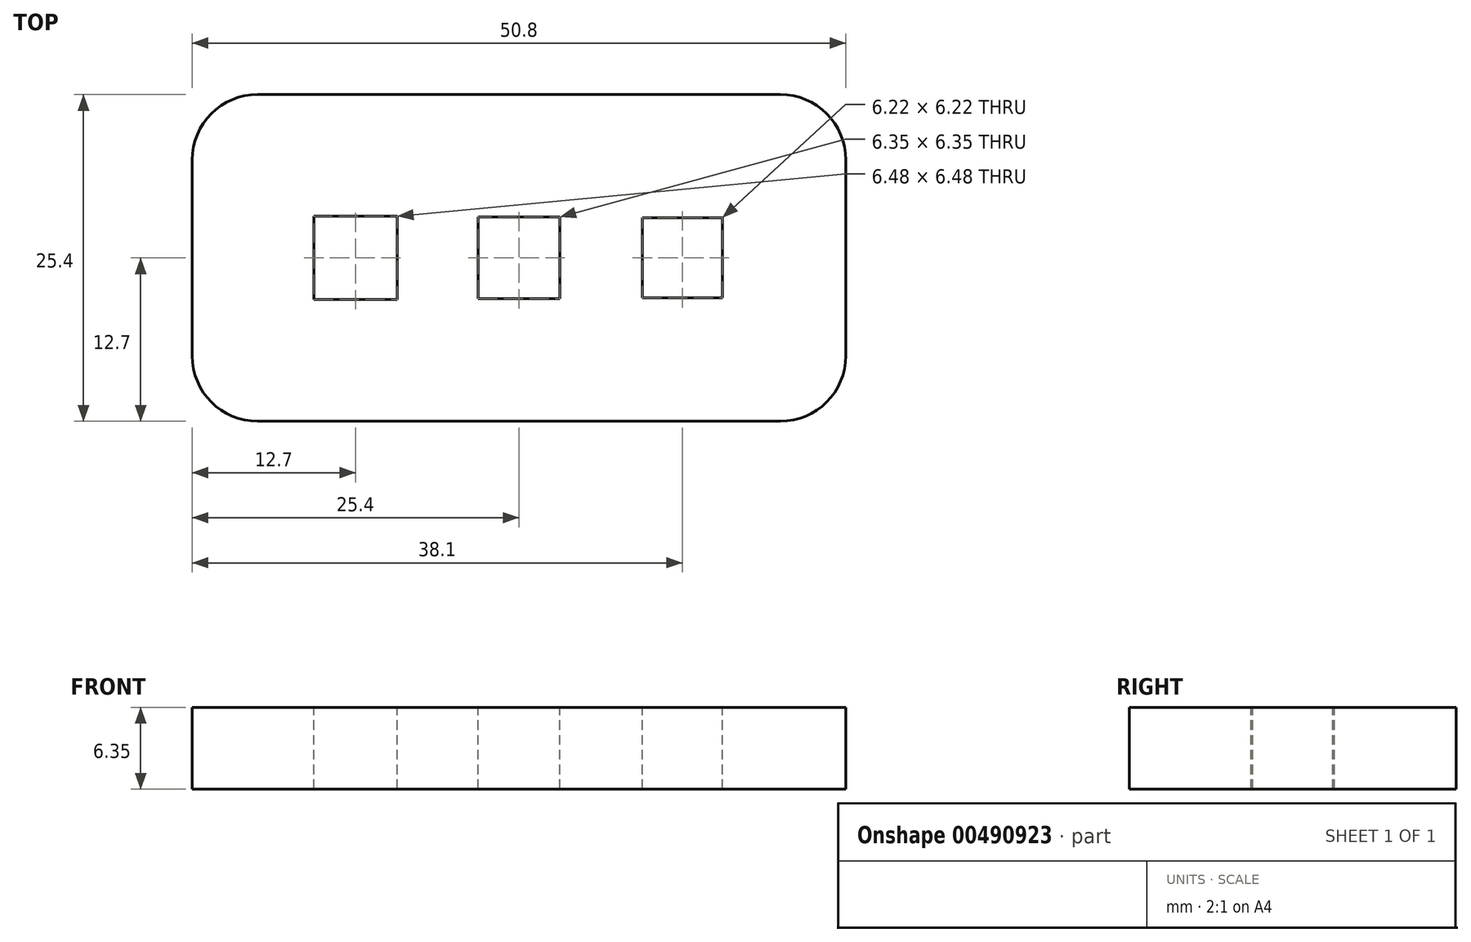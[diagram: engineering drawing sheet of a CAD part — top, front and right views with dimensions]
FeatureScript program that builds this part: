
annotation { "Feature Type Name" : "Feature", "Feature Type Description" : "" }
export const myFeature = defineFeature(function(context is Context, id is Id, definition is map)
    precondition{}
    {
        {
            var Q0;
            Q0=qCreatedBy(makeId("Top.planeOp"),FACE);
            var sketch = newSketch(context, id + "F0", { "sketchPlane" : qUnion([Q0])});
            skLineSegment(sketch, "E0", {"start": v(0, 0) * mm, "end": v(50.8, 0) * mm});
            skLineSegment(sketch, "E1", {"start": v(50.8, 0) * mm, "end": v(50.8, 25.4) * mm});
            skLineSegment(sketch, "E2", {"start": v(50.8, 25.4) * mm, "end": v(0, 25.4) * mm});
            skLineSegment(sketch, "E3", {"start": v(0, 25.4) * mm, "end": v(0, 0) * mm});
            skSolve(sketch);
        }
        {
            var Q0;
            Q0 = qSketchRegion(id + "F0", true);
            extrude(context, id + "F1", {"entities" : qUnion([Q0]), "depth" : 6.35 * mm});
        }
        {
            var Q0;
            Q0=makeQuery(id+"F1.opExtrude","CAP_FACE",FACE,{"disambiguationData":[OSD([sQuery(id+"F0.wireOp",EDGE,"E0"),sQuery(id+"F0.wireOp",EDGE,"E1"),sQuery(id+"F0.wireOp",EDGE,"E2"),sQuery(id+"F0.wireOp",EDGE,"E3")])],"isStart":false});
            var sketch = newSketch(context, id + "F2", { "sketchPlane" : qUnion([Q0])});
            skLineSegment(sketch, "E4", {"start": v(50.8, 12.7) * mm, "end": v(0, 12.7) * mm, "construction": true});
            skLineSegment(sketch, "E5", {"start": v(12.7, 0) * mm, "end": v(12.7, 25.4) * mm, "construction": true});
            skLineSegment(sketch, "E6", {"start": v(25.4, 0) * mm, "end": v(25.4, 25.4) * mm, "construction": true});
            skLineSegment(sketch, "E7", {"start": v(38.1, 0) * mm, "end": v(38.1, 25.4) * mm, "construction": true});
            skLineSegment(sketch, "E8", {"start": v(9.46, 9.46) * mm, "end": v(9.46, 15.94) * mm});
            skLineSegment(sketch, "E9", {"start": v(9.46, 15.94) * mm, "end": v(15.94, 15.94) * mm});
            skLineSegment(sketch, "E10", {"start": v(15.94, 15.94) * mm, "end": v(15.94, 9.46) * mm});
            skLineSegment(sketch, "E11", {"start": v(15.94, 9.46) * mm, "end": v(9.46, 9.46) * mm});
            skLineSegment(sketch, "E12", {"start": v(22.23, 9.53) * mm, "end": v(22.23, 15.88) * mm});
            skLineSegment(sketch, "E13", {"start": v(22.23, 15.88) * mm, "end": v(28.58, 15.88) * mm});
            skLineSegment(sketch, "E14", {"start": v(28.58, 15.88) * mm, "end": v(28.58, 9.53) * mm});
            skLineSegment(sketch, "E15", {"start": v(28.58, 9.53) * mm, "end": v(22.23, 9.53) * mm});
            skLineSegment(sketch, "E16", {"start": v(34.99, 9.59) * mm, "end": v(34.99, 15.81) * mm});
            skLineSegment(sketch, "E17", {"start": v(34.99, 15.81) * mm, "end": v(41.21, 15.81) * mm});
            skLineSegment(sketch, "E18", {"start": v(41.21, 15.81) * mm, "end": v(41.21, 9.59) * mm});
            skLineSegment(sketch, "E19", {"start": v(41.21, 9.59) * mm, "end": v(34.99, 9.59) * mm});
            skSolve(sketch);
        }
        {
            var Q0;
            Q0 = qSketchRegion(id + "F2", true);
            extrude(context, id + "F3", {"entities" : qUnion([Q0]), "operationType" : NewBodyOperationType.REMOVE, "oppositeDirection" : true, "depth" : 25.4 * mm});
        }
        {
            var Q0;
            Q0=makeQuery(id+"F1.opExtrude","SWEPT_EDGE",EDGE,{"disambiguationData":[OSD([sQuery(id+"F0.wireOp",EDGE,"E2"),sQuery(id+"F0.wireOp",EDGE,"E3")])]});
            var Q1;
            Q1=makeQuery(id+"F1.opExtrude","SWEPT_EDGE",EDGE,{"disambiguationData":[OSD([sQuery(id+"F0.wireOp",EDGE,"E0"),sQuery(id+"F0.wireOp",EDGE,"E3")])]});
            var Q2;
            Q2=makeQuery(id+"F1.opExtrude","SWEPT_EDGE",EDGE,{"disambiguationData":[OSD([sQuery(id+"F0.wireOp",EDGE,"E1"),sQuery(id+"F0.wireOp",EDGE,"E2")])]});
            var Q3;
            Q3=makeQuery(id+"F1.opExtrude","SWEPT_EDGE",EDGE,{"disambiguationData":[OSD([sQuery(id+"F0.wireOp",EDGE,"E0"),sQuery(id+"F0.wireOp",EDGE,"E1")])]});
            fillet(context, id + "F4", {"entities" : qUnion([Q0, Q1, Q2, Q3]), "radius" : 5.08 * mm, "tangentPropagation" : true, "allowEdgeOverflow" : false});
        }
    });
